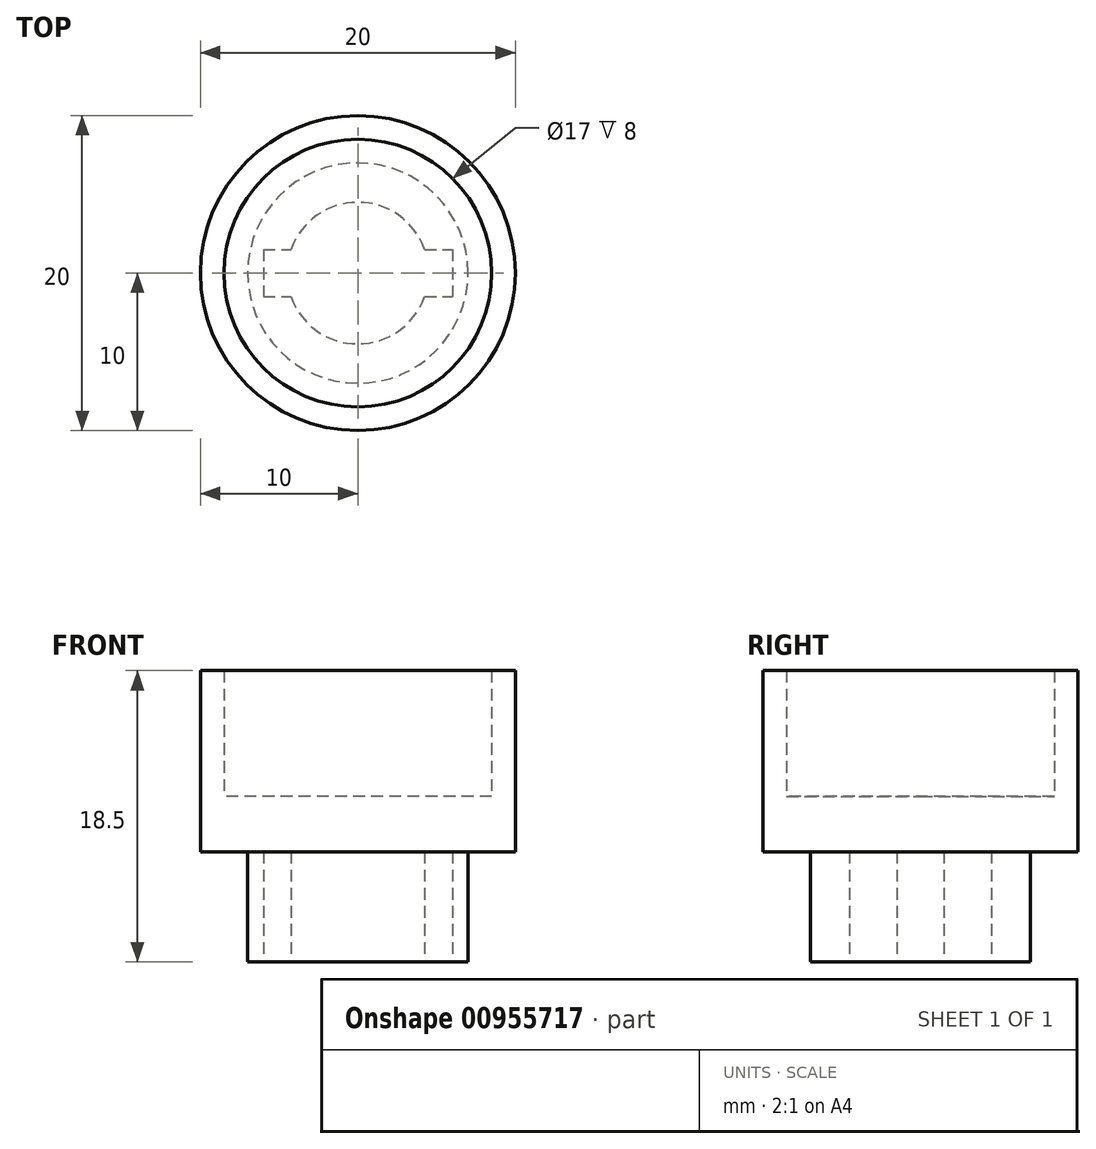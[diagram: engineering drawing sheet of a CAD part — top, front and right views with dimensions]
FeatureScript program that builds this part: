
annotation { "Feature Type Name" : "Feature", "Feature Type Description" : "" }
export const myFeature = defineFeature(function(context is Context, id is Id, definition is map)
    precondition{}
    {
        {
            var Q0;
            Q0=qCreatedBy(makeId("Top.planeOp"),FACE);
            var sketch = newSketch(context, id + "F0", { "sketchPlane" : qUnion([Q0])});
            skCircle(sketch, "E0", {"center": v(0, 0) * mm, "radius": 4.5 * mm});
            skLineSegment(sketch, "E1", {"start": v(0, 0) * mm, "end": v(-6, 0) * mm});
            skLineSegment(sketch, "E2", {"start": v(-6, 0) * mm, "end": v(-6, 1.5) * mm});
            skLineSegment(sketch, "E3", {"start": v(-6, 1.5) * mm, "end": v(6, 1.5) * mm});
            skLineSegment(sketch, "E4", {"start": v(6, 1.5) * mm, "end": v(6, 0) * mm});
            skLineSegment(sketch, "E5", {"start": v(6, 0) * mm, "end": v(0, 0) * mm});
            skLineSegment(sketch, "E6", {"start": v(-6, 0) * mm, "end": v(-6, -1.5) * mm});
            skLineSegment(sketch, "E7", {"start": v(-6, -1.5) * mm, "end": v(6, -1.5) * mm});
            skLineSegment(sketch, "E8", {"start": v(6, -1.5) * mm, "end": v(6, 0) * mm});
            skCircle(sketch, "E9", {"center": v(0, 0) * mm, "radius": 7 * mm});
            skSolve(sketch);
        }
        {
            var Q0;
            {var subQ10=sQuery(id+"F0.wireOp",EDGE,"E2");Q0=makeQuery(id+"F0.imprint","IMPRINT",FACE,{"disambiguationData":[TD([[makeQuery(id+"F0.imprint","IMPRINT",EDGE,{"derivedFrom":subQ10}),1.0]])]});}
            extrude(context, id + "F1", {"entities" : qUnion([Q0]), "depth" : 7 * mm, "offsetDistance" : 25 * mm});
        }
        {
            var Q0;
            Q0=makeQuery(id+"F1.opExtrude","CAP_FACE",FACE,{"disambiguationData":[OSD([sQuery(id+"F0.wireOp",EDGE,"E0"),sQuery(id+"F0.wireOp",EDGE,"E2"),sQuery(id+"F0.wireOp",EDGE,"E3"),sQuery(id+"F0.wireOp",EDGE,"E4"),sQuery(id+"F0.wireOp",EDGE,"E6"),sQuery(id+"F0.wireOp",EDGE,"E7"),sQuery(id+"F0.wireOp",EDGE,"E8"),sQuery(id+"F0.wireOp",EDGE,"E9")])],"isStart":false});
            var sketch = newSketch(context, id + "F2", { "sketchPlane" : qUnion([Q0])});
            skCircle(sketch, "E10", {"center": v(0, 0) * mm, "radius": 8.5 * mm});
            skCircle(sketch, "E11", {"center": v(0, 0) * mm, "radius": 10 * mm});
            skSolve(sketch);
        }
        {
            var Q0;
            {var subQ1=sQuery(id+"F0.wireOp",EDGE,"E2");var subQ4=sQuery(id+"F0.wireOp",EDGE,"E6");Q0=makeQuery(id+"F2.imprint","IMPRINT",FACE,{"disambiguationData":[TD([[makeQuery(id+"F2.imprint","IMPRINT",EDGE,{"derivedFrom":makeQuery(id+"F1.opExtrude","CAP_EDGE",EDGE,{"disambiguationData":[OSD([subQ1,subQ4])],"isStart":false})}),1.0]])]});}
            var Q1;
            Q1=makeQuery(id+"F2.imprint","IMPRINT",FACE,{"disambiguationData":[TD([[makeQuery(id+"F2.imprint","IMPRINT",EDGE,{"derivedFrom":makeQuery(id+"F1.opExtrude","CAP_EDGE",EDGE,{"disambiguationData":[OSD([sQuery(id+"F0.wireOp",EDGE,"E9")])],"isStart":false})}),1.0]])]});
            var Q2;
            Q2=makeQuery(id+"F2.imprint","IMPRINT",FACE,{"disambiguationData":[TD([[makeQuery(id+"F2.imprint","IMPRINT",EDGE,{"derivedFrom":sQuery(id+"F2.wireOp",EDGE,"E10")}),1.0]])]});
            var Q3;
            Q3=makeQuery(id+"F2.imprint","IMPRINT",FACE,{"disambiguationData":[TD([[makeQuery(id+"F2.imprint","IMPRINT",EDGE,{"derivedFrom":sQuery(id+"F2.wireOp",EDGE,"E10")}),-1.0]])]});
            extrude(context, id + "F3", {"entities" : qUnion([Q0, Q1, Q2, Q3]), "operationType" : NewBodyOperationType.ADD, "depth" : 3.5 * mm, "offsetDistance" : 25 * mm});
        }
        {
            var Q0;
            Q0=makeQuery(id+"F3.opExtrude","CAP_FACE",FACE,{"disambiguationData":[OSD([sQuery(id+"F2.wireOp",EDGE,"E11")])],"isStart":false});
            var sketch = newSketch(context, id + "F4", { "sketchPlane" : qUnion([Q0])});
            skCircle(sketch, "E12", {"center": v(0, 0) * mm, "radius": 8.5 * mm});
            skSolve(sketch);
        }
        {
            var Q0;
            Q0=makeQuery(id+"F4.imprint","IMPRINT",FACE,{"disambiguationData":[TD([[makeQuery(id+"F4.imprint","IMPRINT",EDGE,{"derivedFrom":sQuery(id+"F4.wireOp",EDGE,"E12")}),-1.0]])]});
            extrude(context, id + "F5", {"entities" : qUnion([Q0]), "operationType" : NewBodyOperationType.ADD, "depth" : 8 * mm, "offsetDistance" : 25 * mm});
        }
    });
